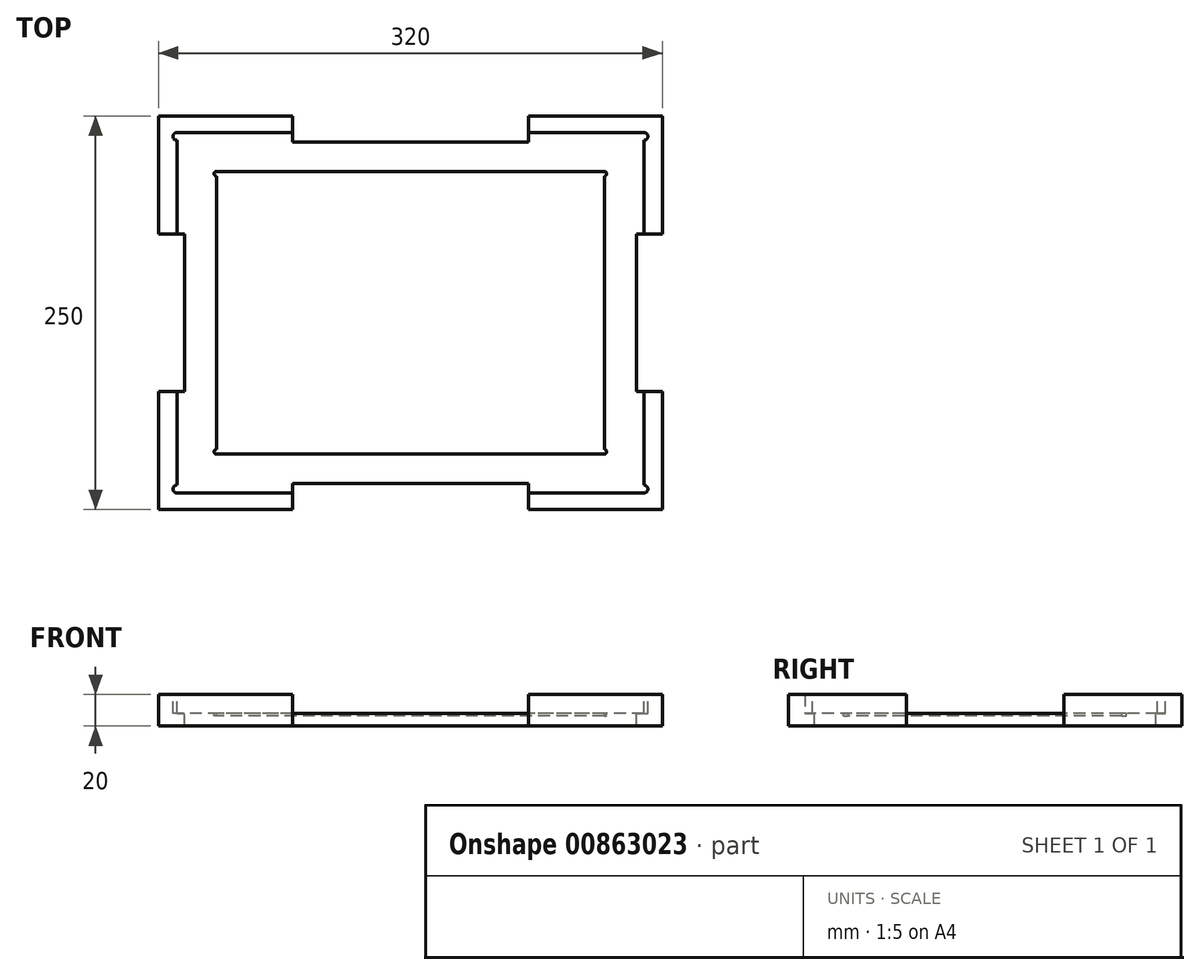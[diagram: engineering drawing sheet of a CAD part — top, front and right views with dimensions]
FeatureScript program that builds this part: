
annotation { "Feature Type Name" : "Feature", "Feature Type Description" : "" }
export const myFeature = defineFeature(function(context is Context, id is Id, definition is map)
    precondition{}
    {
        {
            var Q0;
            Q0=qCreatedBy(makeId("Top.planeOp"),FACE);
            var sketch = newSketch(context, id + "F0", { "sketchPlane" : qUnion([Q0])});
            skLineSegment(sketch, "E0.bottom", {"start": v(160, 125) * mm, "end": v(-160, 125) * mm});
            skLineSegment(sketch, "E0.top", {"start": v(160, -125) * mm, "end": v(-160, -125) * mm});
            skLineSegment(sketch, "E0.left", {"start": v(160, 125) * mm, "end": v(160, -125) * mm});
            skLineSegment(sketch, "E0.right", {"start": v(-160, 125) * mm, "end": v(-160, -125) * mm});
            skPoint(sketch, "E0.middle", {"position": v(0, 0) * mm});
            skSolve(sketch);
        }
        {
            var Q0;
            Q0 = qSketchRegion(id + "F0", true);
            extrude(context, id + "F1", {"entities" : qUnion([Q0]), "depth" : 20 * mm, "offsetDistance" : 25 * mm});
        }
        {
            var Q0;
            Q0=makeQuery(id+"F1.opExtrude","CAP_FACE",FACE,{"disambiguationData":[OSD([sQuery(id+"F0.wireOp",EDGE,"E0.bottom"),sQuery(id+"F0.wireOp",EDGE,"E0.top"),sQuery(id+"F0.wireOp",EDGE,"E0.left"),sQuery(id+"F0.wireOp",EDGE,"E0.right")])],"isStart":false});
            var sketch = newSketch(context, id + "F2", { "sketchPlane" : qUnion([Q0])});
            skLineSegment(sketch, "E1.bottom", {"start": v(148.3, 114.5) * mm, "end": v(-148.3, 114.5) * mm});
            skLineSegment(sketch, "E1.top", {"start": v(148.3, -114.5) * mm, "end": v(-148.3, -114.5) * mm});
            skLineSegment(sketch, "E1.left", {"start": v(148.3, 114.5) * mm, "end": v(148.3, -114.5) * mm});
            skLineSegment(sketch, "E1.right", {"start": v(-148.3, 114.5) * mm, "end": v(-148.3, -114.5) * mm});
            skPoint(sketch, "E1.middle", {"position": v(0, 0) * mm});
            skCircle(sketch, "E2", {"center": v(-148.3, 112) * mm, "radius": 2.5 * mm});
            skCircle(sketch, "E3", {"center": v(148.3, 112) * mm, "radius": 2.5 * mm});
            skCircle(sketch, "E4", {"center": v(148.3, -112) * mm, "radius": 2.5 * mm});
            skCircle(sketch, "E5", {"center": v(-148.3, -112) * mm, "radius": 2.5 * mm});
            skSolve(sketch);
        }
        {
            var Q0;
            Q0 = qSketchRegion(id + "F2", true);
            extrude(context, id + "F3", {"entities" : qUnion([Q0]), "operationType" : NewBodyOperationType.REMOVE, "oppositeDirection" : true, "depth" : 12 * mm, "offsetDistance" : 25 * mm});
        }
        {
            var Q0;
            Q0=makeQuery(id+"F3.boolean.opBoolean","COPY",FACE,{"derivedFrom":makeQuery(id+"F3.opExtrude","CAP_FACE",FACE,{"disambiguationData":[OSD([sQuery(id+"F2.wireOp",EDGE,"E1.bottom"),sQuery(id+"F2.wireOp",EDGE,"E1.top"),sQuery(id+"F2.wireOp",EDGE,"E1.left"),sQuery(id+"F2.wireOp",EDGE,"E1.right")])],"isStart":false})});
            var sketch = newSketch(context, id + "F4", { "sketchPlane" : qUnion([Q0])});
            skLineSegment(sketch, "E6.bottom", {"start": v(123.2, 89.8) * mm, "end": v(-123.2, 89.8) * mm});
            skLineSegment(sketch, "E6.top", {"start": v(123.2, -89.8) * mm, "end": v(-123.2, -89.8) * mm});
            skLineSegment(sketch, "E6.left", {"start": v(123.2, 89.8) * mm, "end": v(123.2, -89.8) * mm});
            skLineSegment(sketch, "E6.right", {"start": v(-123.2, 89.8) * mm, "end": v(-123.2, -89.8) * mm});
            skPoint(sketch, "E6.middle", {"position": v(0, 0) * mm});
            skCircle(sketch, "E7", {"center": v(-123.2, 88.3) * mm, "radius": 1.5 * mm});
            skCircle(sketch, "E8", {"center": v(123.2, 88.3) * mm, "radius": 1.5 * mm});
            skCircle(sketch, "E9", {"center": v(123.2, -88.3) * mm, "radius": 1.5 * mm});
            skCircle(sketch, "E10", {"center": v(-123.2, -88.3) * mm, "radius": 1.5 * mm});
            skSolve(sketch);
        }
        {
            var Q0;
            Q0 = qSketchRegion(id + "F4", true);
            extrude(context, id + "F5", {"entities" : qUnion([Q0]), "operationType" : NewBodyOperationType.REMOVE, "oppositeDirection" : true, "depth" : 1.6 * mm, "offsetDistance" : 25 * mm});
        }
        {
            var Q0;
            Q0=makeQuery(id+"F1.opExtrude","CAP_FACE",FACE,{"disambiguationData":[OSD([sQuery(id+"F0.wireOp",EDGE,"E0.bottom"),sQuery(id+"F0.wireOp",EDGE,"E0.top"),sQuery(id+"F0.wireOp",EDGE,"E0.left"),sQuery(id+"F0.wireOp",EDGE,"E0.right")])],"isStart":false});
            var sketch = newSketch(context, id + "F6", { "sketchPlane" : qUnion([Q0])});
            skLineSegment(sketch, "E11.bottom", {"start": v(-176.5, 50) * mm, "end": v(-143.5, 50) * mm});
            skLineSegment(sketch, "E11.top", {"start": v(-176.5, -50) * mm, "end": v(-143.5, -50) * mm});
            skLineSegment(sketch, "E11.left", {"start": v(-176.5, 50) * mm, "end": v(-176.5, -50) * mm});
            skLineSegment(sketch, "E11.right", {"start": v(-143.5, 50) * mm, "end": v(-143.5, -50) * mm});
            skPoint(sketch, "E11.middle", {"position": v(-160, 0) * mm});
            skLineSegment(sketch, "E12.bottom", {"start": v(-75, 141.5) * mm, "end": v(75, 141.5) * mm});
            skLineSegment(sketch, "E12.top", {"start": v(-75, 108.5) * mm, "end": v(75, 108.5) * mm});
            skLineSegment(sketch, "E12.left", {"start": v(-75, 141.5) * mm, "end": v(-75, 108.5) * mm});
            skLineSegment(sketch, "E12.right", {"start": v(75, 141.5) * mm, "end": v(75, 108.5) * mm});
            skPoint(sketch, "E12.middle", {"position": v(0, 125) * mm});
            skLineSegment(sketch, "E13.bottom", {"start": v(143.5, 50) * mm, "end": v(176.5, 50) * mm});
            skLineSegment(sketch, "E13.top", {"start": v(143.5, -50) * mm, "end": v(176.5, -50) * mm});
            skLineSegment(sketch, "E13.left", {"start": v(143.5, 50) * mm, "end": v(143.5, -50) * mm});
            skLineSegment(sketch, "E13.right", {"start": v(176.5, 50) * mm, "end": v(176.5, -50) * mm});
            skPoint(sketch, "E13.middle", {"position": v(160, 0) * mm});
            skLineSegment(sketch, "E14.bottom", {"start": v(-75, -141.5) * mm, "end": v(75, -141.5) * mm});
            skLineSegment(sketch, "E14.top", {"start": v(-75, -108.5) * mm, "end": v(75, -108.5) * mm});
            skLineSegment(sketch, "E14.left", {"start": v(-75, -141.5) * mm, "end": v(-75, -108.5) * mm});
            skLineSegment(sketch, "E14.right", {"start": v(75, -141.5) * mm, "end": v(75, -108.5) * mm});
            skPoint(sketch, "E14.middle", {"position": v(0, -125) * mm});
            skSolve(sketch);
        }
        {
            var Q0;
            Q0 = qSketchRegion(id + "F6", true);
            extrude(context, id + "F7", {"entities" : qUnion([Q0]), "operationType" : NewBodyOperationType.REMOVE, "endBound" : BoundingType.THROUGH_ALL, "oppositeDirection" : true, "depth" : 25 * mm, "offsetDistance" : 25 * mm});
        }
    });
